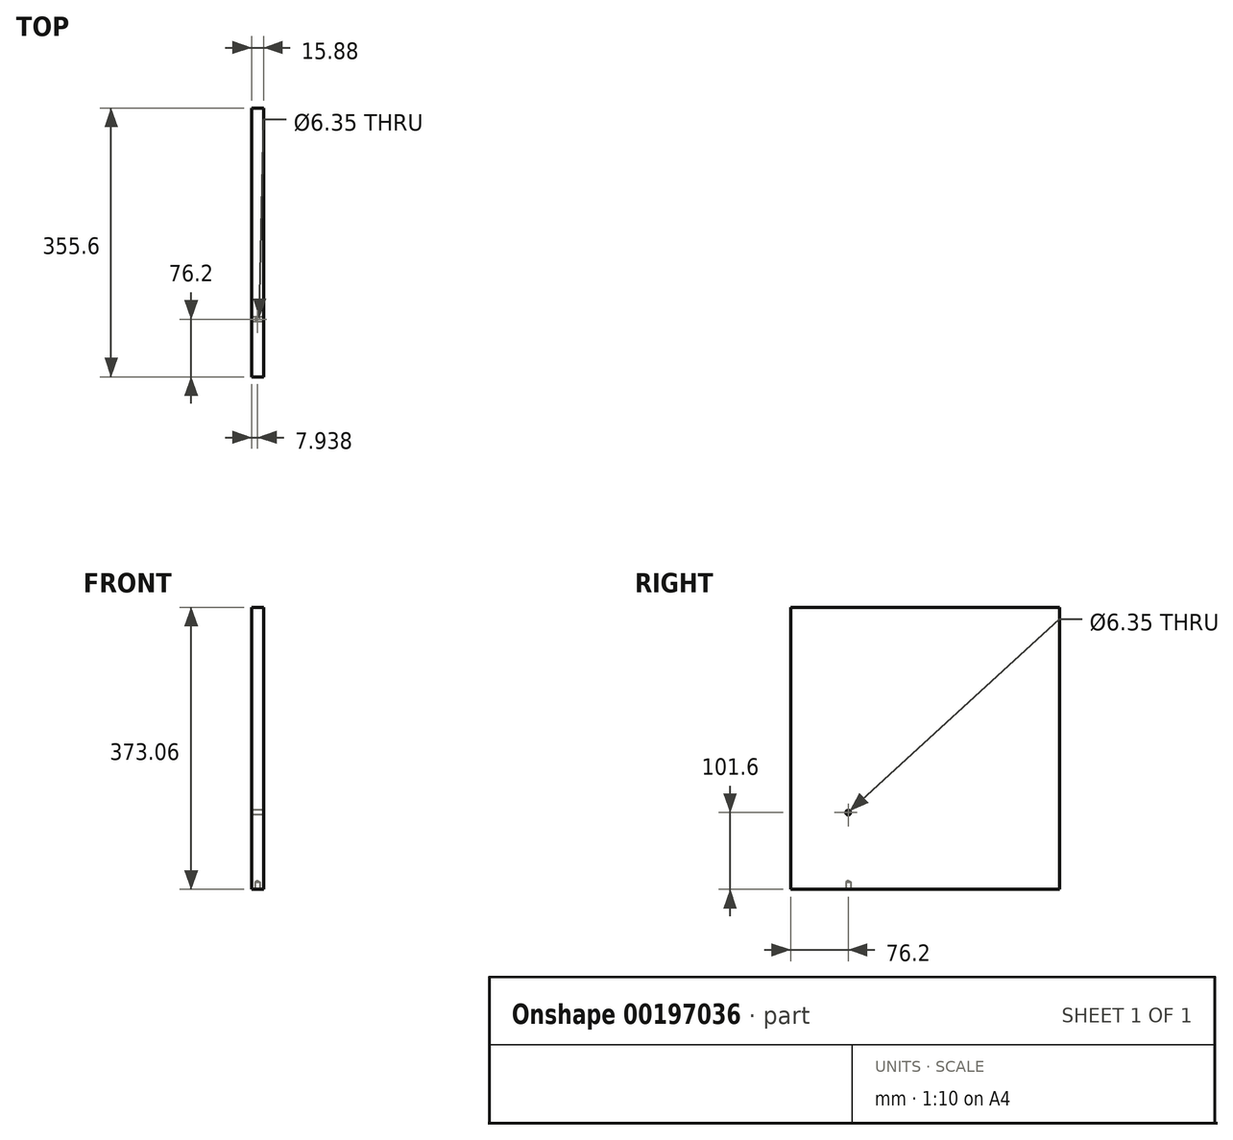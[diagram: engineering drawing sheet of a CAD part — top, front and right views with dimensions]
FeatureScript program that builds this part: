
annotation { "Feature Type Name" : "Feature", "Feature Type Description" : "" }
export const myFeature = defineFeature(function(context is Context, id is Id, definition is map)
    precondition{}
    {
        {
            var Q0;
            Q0=qCreatedBy(makeId("Right.planeOp"),FACE);
            var sketch = newSketch(context, id + "F0", { "sketchPlane" : qUnion([Q0])});
            skLineSegment(sketch, "E0.bottom", {"start": v(0, 0) * mm, "end": v(355.6, 0) * mm});
            skLineSegment(sketch, "E0.top", {"start": v(0, 373.06) * mm, "end": v(355.6, 373.06) * mm});
            skLineSegment(sketch, "E0.left", {"start": v(0, 0) * mm, "end": v(0, 373.06) * mm});
            skLineSegment(sketch, "E0.right", {"start": v(355.6, 0) * mm, "end": v(355.6, 373.06) * mm});
            skSolve(sketch);
        }
        {
            var Q0;
            Q0=makeQuery(id+"F0.imprint","IMPRINT",FACE,{"disambiguationData":[TD([[makeQuery(id+"F0.imprint","IMPRINT",EDGE,{"derivedFrom":sQuery(id+"F0.wireOp",EDGE,"E0.bottom")}),1.0]])]});
            extrude(context, id + "F1", {"entities" : qUnion([Q0]), "depth" : 15.88 * mm});
        }
        {
            var Q0;
            Q0=makeQuery(id+"F1.opExtrude","SWEPT_FACE",FACE,{"disambiguationData":[OSD([sQuery(id+"F0.wireOp",EDGE,"E0.bottom")])]});
            var sketch = newSketch(context, id + "F2", { "sketchPlane" : qUnion([Q0])});
            skLineSegment(sketch, "E1", {"start": v(7.94, 0) * mm, "end": v(7.94, -355.6) * mm, "construction": true});
            skPoint(sketch, "E2", {"position": v(7.94, -279.4) * mm});
            skPoint(sketch, "E3", {"position": v(7.94, -76.2) * mm});
            skSolve(sketch);
        }
        {
            var Q0;
            Q0=sQuery(id+"F2.wireOp",VERTEX,"E3");
            var Q1;
            Q1=makeQuery(id+"F1.opExtrude","SWEPT_BODY",BODY,{"disambiguationData":[OSD([sQuery(id+"F0.wireOp",EDGE,"E0.bottom"),sQuery(id+"F0.wireOp",EDGE,"E0.top"),sQuery(id+"F0.wireOp",EDGE,"E0.left"),sQuery(id+"F0.wireOp",EDGE,"E0.right")])]});
            hole(context, id + "F3", {"style" : HoleStyle.SIMPLE, "endStyle" : HoleEndStyle.BLIND, "holeDiameter" : 6.35 * mm, "holeDepth" : 9.52 * mm, "locations" : qUnion([Q0]), "scope" : qUnion([Q1])});
        }
        {
            var Q0;
            Q0=makeQuery(id+"F1.opExtrude","CAP_FACE",FACE,{"disambiguationData":[OSD([sQuery(id+"F0.wireOp",EDGE,"E0.bottom"),sQuery(id+"F0.wireOp",EDGE,"E0.top"),sQuery(id+"F0.wireOp",EDGE,"E0.left"),sQuery(id+"F0.wireOp",EDGE,"E0.right")])],"isStart":true});
            var sketch = newSketch(context, id + "F4", { "sketchPlane" : qUnion([Q0])});
            skLineSegment(sketch, "E4", {"start": v(0, 101.6) * mm, "end": v(-355.6, 101.6) * mm, "construction": true});
            skPoint(sketch, "E5", {"position": v(-76.2, 101.6) * mm});
            skSolve(sketch);
        }
        {
            var Q0;
            Q0=sQuery(id+"F4.wireOp",VERTEX,"E5");
            var Q1;
            Q1=makeQuery(id+"F1.opExtrude","SWEPT_BODY",BODY,{"disambiguationData":[OSD([sQuery(id+"F0.wireOp",EDGE,"E0.bottom"),sQuery(id+"F0.wireOp",EDGE,"E0.top"),sQuery(id+"F0.wireOp",EDGE,"E0.left"),sQuery(id+"F0.wireOp",EDGE,"E0.right")])]});
            hole(context, id + "F5", {"style" : HoleStyle.SIMPLE, "endStyle" : HoleEndStyle.THROUGH, "holeDiameter" : 6.35 * mm, "locations" : qUnion([Q0]), "scope" : qUnion([Q1]), "isTappedThrough" : true});
        }
    });
